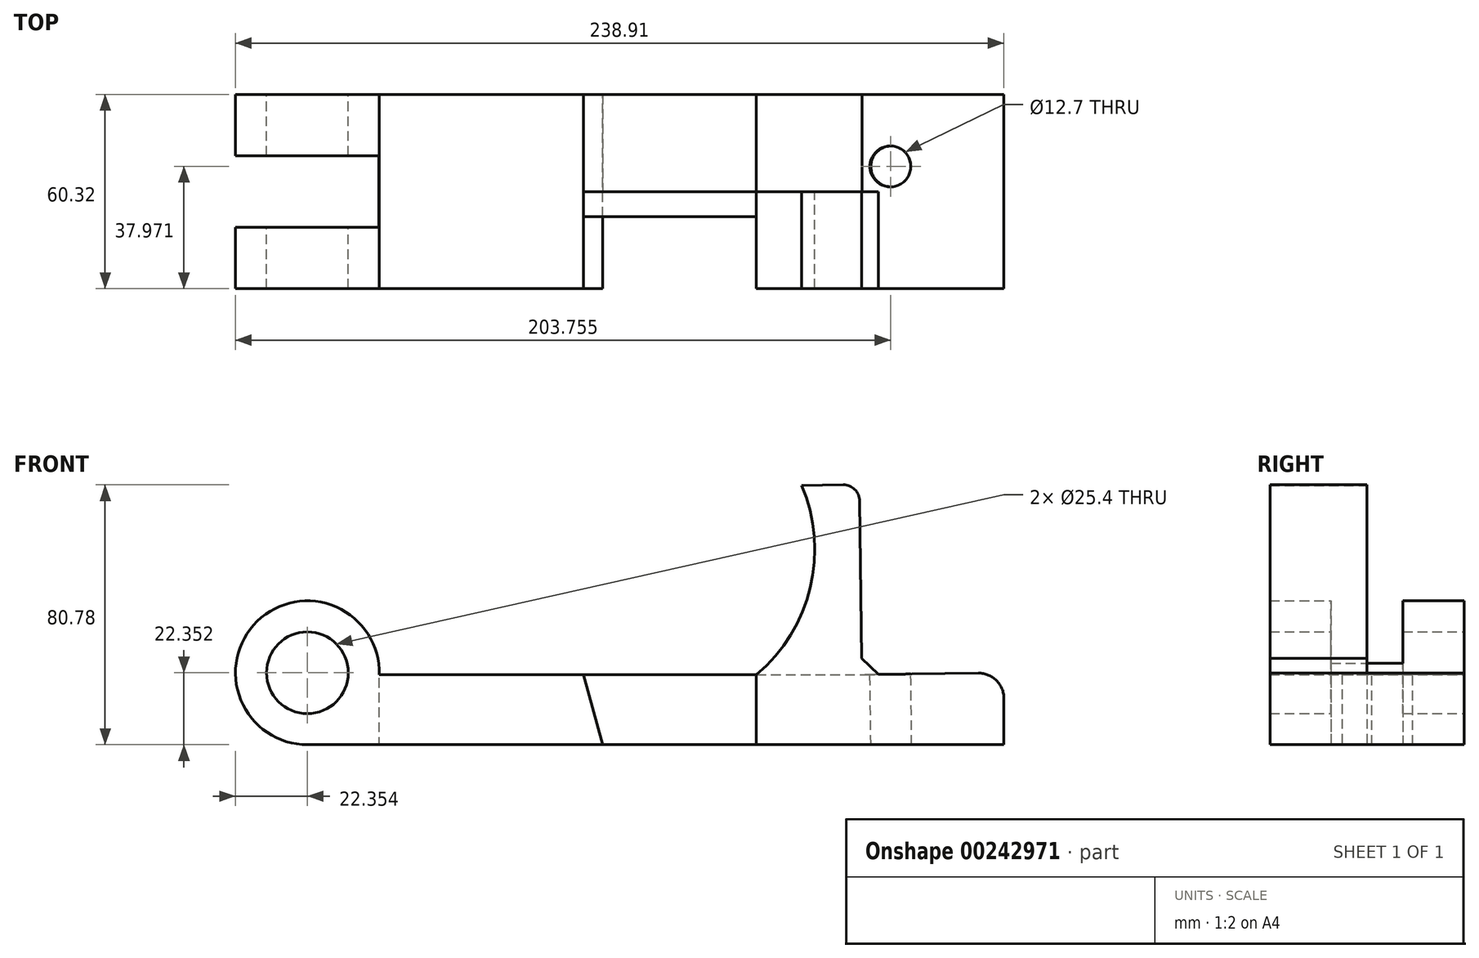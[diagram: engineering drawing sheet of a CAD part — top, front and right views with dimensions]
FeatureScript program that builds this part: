
annotation { "Feature Type Name" : "Feature", "Feature Type Description" : "" }
export const myFeature = defineFeature(function(context is Context, id is Id, definition is map)
    precondition{}
    {
        {
            var Q0;
            Q0=qCreatedBy(makeId("Front.planeOp"),FACE);
            var sketch = newSketch(context, id + "F0", { "sketchPlane" : qUnion([Q0])});
            skLineSegment(sketch, "E0.bottom", {"start": v(0, 0) * mm, "end": v(-91.85, 0) * mm});
            skLineSegment(sketch, "E0.right", {"start": v(-91.85, 0) * mm, "end": v(-91.85, 22.35) * mm});
            skCircle(sketch, "E1", {"center": v(-91.85, 22.35) * mm, "radius": 12.7 * mm});
            skCircle(sketch, "E2", {"center": v(-91.85, 22.35) * mm, "radius": 22.35 * mm});
            skLineSegment(sketch, "E3", {"start": v(0, 0) * mm, "end": v(-6, 21.78) * mm});
            skLineSegment(sketch, "E4", {"start": v(47.75, 21.78) * mm, "end": v(47.75, 0) * mm});
            skLineSegment(sketch, "E5", {"start": v(47.75, 0) * mm, "end": v(0, 0) * mm});
            skLineSegment(sketch, "E6", {"start": v(-6, 21.78) * mm, "end": v(-69.5, 21.78) * mm});
            skLineSegment(sketch, "E7", {"start": v(-6, 21.78) * mm, "end": v(47.75, 21.78) * mm});
            skLineSegment(sketch, "E8", {"start": v(47.75, 0) * mm, "end": v(124.71, 0) * mm});
            skLineSegment(sketch, "E9", {"start": v(124.71, 0) * mm, "end": v(124.71, 22.35) * mm});
            skLineSegment(sketch, "E10", {"start": v(124.71, 22.35) * mm, "end": v(80.6, 21.78) * mm});
            skLineSegment(sketch, "E11", {"start": v(80.6, 21.78) * mm, "end": v(79.83, 80.85) * mm});
            skLineSegment(sketch, "E12", {"start": v(79.83, 80.85) * mm, "end": v(61.83, 80.62) * mm});
            skLineSegment(sketch, "E13", {"start": v(47.75, 21.78) * mm, "end": v(80.6, 21.78) * mm});
            skArc(sketch, "E14", {"start": v(47.75, 21.78) * mm, "mid": v(64.5, 48.87) * mm, "end": v(61.83, 80.62) * mm});
            skSolve(sketch);
        }
        {
            var Q0;
            Q0=makeQuery(id+"F0.imprint","IMPRINT",FACE,{"disambiguationData":[TD([[makeQuery(id+"F0.imprint","IMPRINT",EDGE,{"derivedFrom":sQuery(id+"F0.wireOp",EDGE,"E1")}),-1.0]])]});
            var Q1;
            {var subQ0=sQuery(id+"F0.wireOp",EDGE,"E0.bottom");Q1=makeQuery(id+"F0.imprint","IMPRINT",FACE,{"disambiguationData":[TD([[makeQuery(id+"F0.imprint","IMPRINT",EDGE,{"derivedFrom":subQ0}),-1.0]])]});}
            var Q2;
            Q2=makeQuery(id+"F0.imprint","IMPRINT",FACE,{"disambiguationData":[TD([[makeQuery(id+"F0.imprint","IMPRINT",EDGE,{"derivedFrom":sQuery(id+"F0.wireOp",EDGE,"E4")}),1.0]])]});
            extrude(context, id + "F1", {"entities" : qUnion([Q0, Q1, Q2]), "endBound" : BoundingType.SYMMETRIC, "depth" : 60.32 * mm});
        }
        {
            var Q0;
            Q0=makeQuery(id+"F0.imprint","IMPRINT",FACE,{"disambiguationData":[TD([[makeQuery(id+"F0.imprint","IMPRINT",EDGE,{"derivedFrom":sQuery(id+"F0.wireOp",EDGE,"E11")}),1.0]])]});
            extrude(context, id + "F2", {"entities" : qUnion([Q0]), "operationType" : NewBodyOperationType.ADD, "depth" : 30.16 * mm});
        }
        {
            var Q0;
            Q0=makeQuery(id+"F1.opExtrude","SWEPT_FACE",FACE,{"disambiguationData":[OSD([sQuery(id+"F0.wireOp",EDGE,"E10")])]});
            var sketch = newSketch(context, id + "F3", { "sketchPlane" : qUnion([Q0])});
            skLineSegment(sketch, "E15", {"start": v(125, 30.16) * mm, "end": v(89.69, 30.16) * mm});
            skLineSegment(sketch, "E16", {"start": v(89.69, 30.16) * mm, "end": v(89.69, 7.81) * mm});
            skCircle(sketch, "E17", {"center": v(89.69, 7.81) * mm, "radius": 6.35 * mm});
            skSolve(sketch);
        }
        {
            var Q0;
            Q0=makeQuery(id+"F3.imprint","IMPRINT",FACE,{"disambiguationData":[TD([[makeQuery(id+"F3.imprint","IMPRINT",EDGE,{"derivedFrom":sQuery(id+"F3.wireOp",EDGE,"E17")}),1.0]])]});
            extrude(context, id + "F4", {"entities" : qUnion([Q0]), "operationType" : NewBodyOperationType.REMOVE, "oppositeDirection" : true, "depth" : 80.77 * mm});
        }
        {
            var Q0;
            Q0=makeQuery(id+"F0.imprint","IMPRINT",FACE,{"disambiguationData":[TD([[makeQuery(id+"F0.imprint","IMPRINT",EDGE,{"derivedFrom":sQuery(id+"F0.wireOp",EDGE,"E1")}),1.0]])]});
            var sketch = newSketch(context, id + "F5", { "sketchPlane" : qUnion([Q0])});
            skLineSegment(sketch, "E18.bottom", {"start": v(-70.27, 57.82) * mm, "end": v(-115.48, 57.82) * mm});
            skLineSegment(sketch, "E19.bottom", {"start": v(-69.7, 45.99) * mm, "end": v(-114.9, 45.99) * mm});
            skLineSegment(sketch, "E19.top", {"start": v(-69.7, -45.99) * mm, "end": v(-114.9, -45.99) * mm});
            skLineSegment(sketch, "E19.left", {"start": v(-69.7, 45.99) * mm, "end": v(-69.7, -45.99) * mm});
            skLineSegment(sketch, "E19.right", {"start": v(-114.9, 45.99) * mm, "end": v(-114.9, -45.99) * mm});
            skPoint(sketch, "E19.middle", {"position": v(-92.3, 0) * mm});
            skSolve(sketch);
        }
        {
            var Q0;
            Q0=qSketchRegion(id+"F5",true);
            extrude(context, id + "F6", {"entities" : qUnion([Q0]), "operationType" : NewBodyOperationType.REMOVE, "endBound" : BoundingType.SYMMETRIC, "depth" : 22.33 * mm});
        }
        {
            var Q0;
            Q0=makeQuery(id+"F0.imprint","IMPRINT",FACE,{"disambiguationData":[TD([[makeQuery(id+"F0.imprint","IMPRINT",EDGE,{"derivedFrom":sQuery(id+"F0.wireOp",EDGE,"E3")}),-1.0]])]});
            extrude(context, id + "F7", {"entities" : qUnion([Q0]), "oppositeDirection" : true, "depth" : 30.16 * mm});
        }
        {
            var Q0;
            Q0=makeQuery(id+"F0.imprint","IMPRINT",FACE,{"disambiguationData":[TD([[makeQuery(id+"F0.imprint","IMPRINT",EDGE,{"derivedFrom":sQuery(id+"F0.wireOp",EDGE,"E3")}),-1.0]])]});
            extrude(context, id + "F8", {"entities" : qUnion([Q0]), "depth" : 7.8 * mm});
        }
        {
            var Q0;
            Q0=makeQuery(id+"F2.opExtrude","SWEPT_EDGE",EDGE,{"disambiguationData":[OSD([sQuery(id+"F0.wireOp",EDGE,"E11"),sQuery(id+"F0.wireOp",EDGE,"E12")])]});
            fillet(context, id + "F9", {"entities" : qUnion([Q0]), "radius" : 5.08 * mm, "tangentPropagation" : true, "allowEdgeOverflow" : false});
        }
        {
            var Q0;
            Q0=makeQuery(id+"F1.opExtrude","SWEPT_EDGE",EDGE,{"disambiguationData":[OSD([sQuery(id+"F0.wireOp",EDGE,"E9"),sQuery(id+"F0.wireOp",EDGE,"E10")])]});
            fillet(context, id + "F10", {"entities" : qUnion([Q0]), "radius" : 7.87 * mm, "tangentPropagation" : true, "allowEdgeOverflow" : false});
        }
        {
            var Q0;
            {var subQ0=sQuery(id+"F0.wireOp",EDGE,"E13");var subQ1=sQuery(id+"F0.wireOp",EDGE,"E11");var subQ2=sQuery(id+"F0.wireOp",EDGE,"E10");Q0=makeQuery(id+"F2.boolean.opBoolean","MERGE",EDGE,{"derivedFrom":[makeQuery(id+"F1.opExtrude","SWEPT_EDGE",EDGE,{"disambiguationData":[OSD([subQ2,subQ1,subQ0])]}),makeQuery(id+"F2.opExtrude","SWEPT_EDGE",EDGE,{"disambiguationData":[OSD([subQ2,subQ1,subQ0])]})]});}
            chamfer(context, id + "F11", {"entities" : qUnion([Q0]), "width" : 5.08 * mm, "tangentPropagation" : true});
        }
    });
